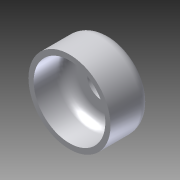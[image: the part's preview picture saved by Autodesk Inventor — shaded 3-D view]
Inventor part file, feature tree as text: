
AUTODESK INVENTOR PART (.ipt)
format: ipt  version: 2014 SP1 (Build 180222100, 222)  size: 133,632 bytes
history: native  units: in
note: dims shown in document units (in); Inventor stores cm internally (conversion verified against a paired STEP export)
features: extrude x3, fillet x2, sketch x1
ambient origin geometry x8: Origin, YZ Plane, XZ Plane, XY Plane, X Axis, Y Axis, Z Axis, Center Point
bodies: Solid1 (feature_tree)
feature tree (6):
  sketch  "Sketch1"  dims[d0=1.66in d1=1.9in d2=0.75in d3=0.0in d4=0.2in d5=0.0in d6=0.25in d7=0.25in d8=0.6875in d9=0.2in d10=0.0in]
  extrude  "Extrusion1"  Depth=0.2in
  extrude  "Extrusion2"  Depth=0.75in TaperAngle=0.0deg
  fillet  "Fillet1"  Radius=0.2in
  fillet  "Fillet2"  Radius=0.25in
  extrude  "Extrusion3"  Depth=0.25in
